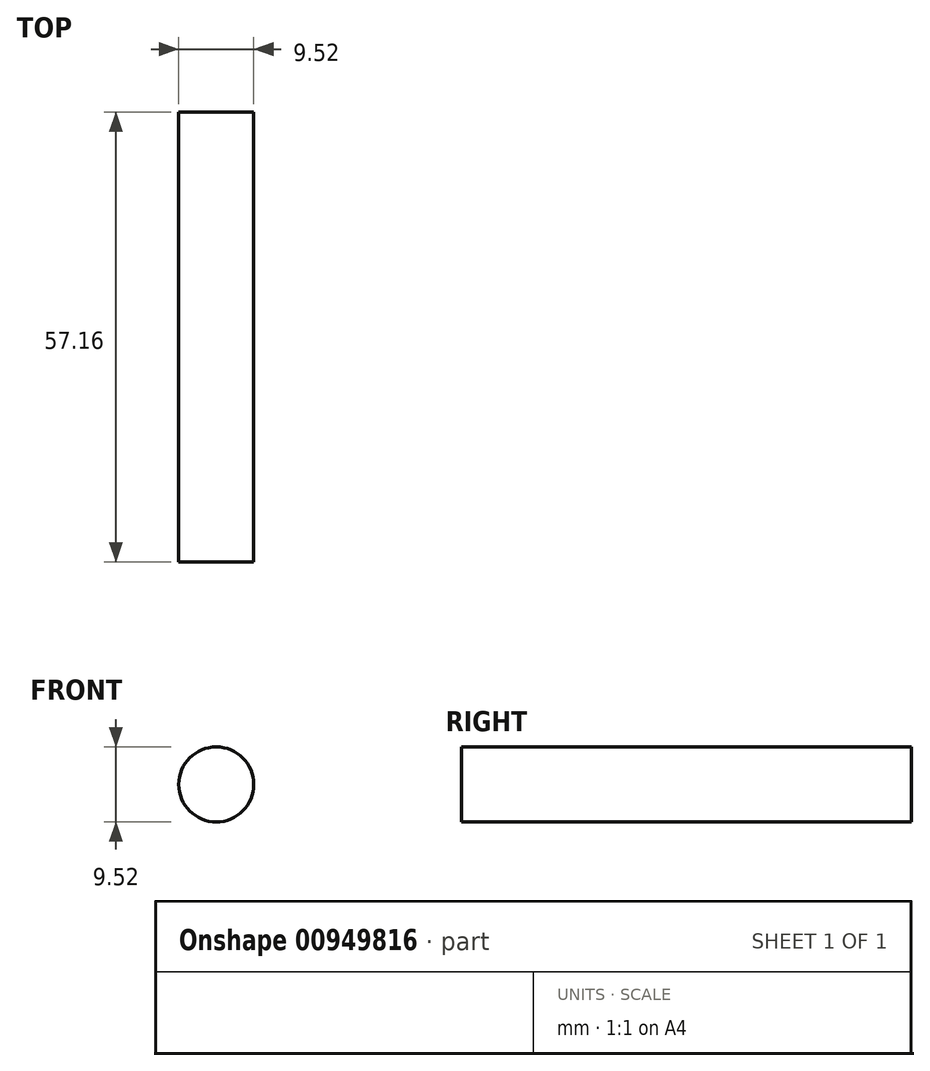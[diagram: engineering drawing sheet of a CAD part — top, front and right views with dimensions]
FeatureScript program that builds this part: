
annotation { "Feature Type Name" : "Feature", "Feature Type Description" : "" }
export const myFeature = defineFeature(function(context is Context, id is Id, definition is map)
    precondition{}
    {
        {
            var Q0;
            Q0=qCreatedBy(makeId("Right.planeOp"),FACE);
            var sketch = newSketch(context, id + "F0", { "sketchPlane" : qUnion([Q0])});
            skLineSegment(sketch, "E0.bottom", {"start": v(-28.58, 0) * mm, "end": v(28.58, 0) * mm});
            skLineSegment(sketch, "E0.top", {"start": v(-28.58, 4.76) * mm, "end": v(28.58, 4.76) * mm});
            skLineSegment(sketch, "E0.left", {"start": v(-28.58, 0) * mm, "end": v(-28.58, 4.76) * mm});
            skLineSegment(sketch, "E0.right", {"start": v(28.58, 0) * mm, "end": v(28.58, 4.76) * mm});
            skSolve(sketch);
        }
        {
            var Q0;
            Q0 = qSketchRegion(id + "F0", true);
            var Q1;
            Q1=sQuery(id+"F0.wireOp",EDGE,"E0.bottom");
            revolve(context, id + "F1", {"surfaceOperationType" : NewSurfaceOperationType.NEW, "entities" : qUnion([Q0]), "axis" : qUnion([Q1]), "revolveType" : RevolveType.FULL});
        }
    });
